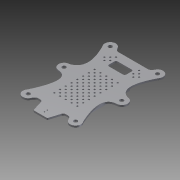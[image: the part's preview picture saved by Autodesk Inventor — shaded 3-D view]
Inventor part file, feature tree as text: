
AUTODESK INVENTOR PART (.ipt)
format: ipt  version: 2015 (Build 190159000, 159)  size: 695,808 bytes
history: native  units: mm
features: sketch x3, extrude x2, hole x2
ambient origin geometry x8: Origin, YZ Plane, XZ Plane, XY Plane, X Axis, Y Axis, Z Axis, Center Point
bodies: Solid1 (feature_tree)
feature tree (7):
  sketch  "Sketch1"  dims[d0=10.0mm d1=6.5mm d2=6.5mm d3=6.5mm d4=6.5mm d5=6.5mm d6=12.0mm d7=2.0mm d8=2.0mm d9=5.0mm d10=5.0mm d11=71.014083mm d12=41.0mm d13=3.0mm d14=3.0mm d15=3.0mm d16=3.0mm d17=3.0mm d18=3.0mm d19=3.0mm d20=3.0mm d21=10.0mm d22=3.0mm d23=3.0mm d24=3.0mm d25=10.0mm d26=12.5mm d27=12.5mm d28=12.5mm d29=12.5mm d30=8.00764mm d31=17.45764mm d32=8.00764mm d33=12.118872mm d34=2.0mm d35=10.0mm d36=10.0mm d37=10.0mm d38=10.0mm d39=10.0mm d40=10.0mm d41=10.0mm d42=10.0mm d43=3.0mm d44=3.0mm d45=3.0mm d46=3.0mm d47=18.0mm d48=5.0mm d49=1.0mm d50=18.0mm d51=18.0mm d52=10.0mm d53=10.0mm d54=10.0mm d55=6.5mm d56=3.0mm d57=3.0mm d58=3.0mm d59=3.0mm d60=3.0mm d61=3.0mm d62=3.0mm d63=10.0mm d64=3.0mm d65=3.0mm d66=3.0mm d67=10.0mm d68=3.0mm d69=3.0mm d70=3.0mm d71=10.0mm d72=3.0mm d73=3.0mm d74=3.0mm d75=10.0mm d76=3.0mm d77=3.0mm d78=3.0mm d79=10.0mm d80=3.0mm d81=3.0mm d82=3.0mm d83=10.0mm d84=3.0mm d85=3.0mm d86=3.0mm d87=10.0mm d88=3.0mm d89=3.0mm d90=3.0mm d91=10.0mm d92=3.0mm d93=3.0mm d94=3.0mm d95=10.0mm d96=3.0mm d97=0.0mm]
  extrude  "Extrusion1"  Depth=10.0mm TaperAngle=0.0deg
  hole  "Hole1"  [1 undecoded]
  hole  "Hole2"  [1 undecoded]
  extrude  "Extrusion2"  [1 undecoded]
  sketch  "Sketch2"  dims[d98=10.0mm d99=6.5mm d100=6.5mm d101=6.5mm d102=6.5mm d103=6.5mm d104=12.0mm d105=2.0mm d106=2.0mm d107=5.0mm d108=5.0mm d109=71.014083mm d110=41.0mm d111=3.0mm d112=3.0mm d113=3.0mm d114=3.0mm d115=3.0mm d116=3.0mm d117=3.0mm d118=3.0mm d119=10.0mm d120=3.0mm d121=3.0mm d122=3.0mm d123=10.0mm d124=12.5mm d125=12.5mm d126=12.5mm d127=12.5mm d128=8.00764mm d129=17.45764mm d130=8.00764mm d131=12.118872mm d132=2.0mm d133=10.0mm d134=10.0mm d135=10.0mm d136=10.0mm d137=10.0mm d138=10.0mm d139=10.0mm d140=10.0mm d141=3.0mm d142=3.0mm d143=3.0mm d144=3.0mm d145=18.0mm d146=5.0mm d147=1.0mm d148=18.0mm d149=18.0mm d150=10.0mm d151=10.0mm d152=10.0mm d153=6.5mm d154=3.0mm d155=3.0mm d156=3.0mm d157=3.0mm d158=3.0mm d159=3.0mm d160=3.0mm d161=10.0mm d162=3.0mm d163=3.0mm d164=3.0mm d165=10.0mm d166=3.0mm d167=3.0mm d168=3.0mm d169=10.0mm d170=3.0mm d171=3.0mm d172=3.0mm d173=10.0mm d174=3.0mm d175=3.0mm d176=3.0mm d177=10.0mm d178=3.0mm d179=3.0mm d180=3.0mm d181=10.0mm d182=3.0mm d183=3.0mm d184=3.0mm d185=10.0mm d186=3.0mm d187=3.0mm d188=3.0mm d189=10.0mm d190=3.0mm d191=3.0mm d192=3.0mm d193=10.0mm d194=6.5mm d195=6.0mm d196=4.0mm d197=2.0mm d198=90.0deg d199=8.0mm d200=20.594885mm]
  sketch  "Sketch3"  dims[d201=10.0mm d202=6.5mm d203=6.5mm d204=6.5mm d205=6.5mm d206=6.5mm d207=12.0mm d208=2.0mm d209=2.0mm d210=5.0mm d211=5.0mm d212=71.014083mm d213=41.0mm d214=3.0mm d215=3.0mm d216=3.0mm d217=3.0mm d218=3.0mm d219=3.0mm d220=3.0mm d221=3.0mm d222=10.0mm d223=3.0mm d224=3.0mm d225=3.0mm d226=10.0mm d227=12.5mm d228=12.5mm d229=12.5mm d230=12.5mm d231=8.00764mm d232=17.45764mm d233=8.00764mm d234=12.118872mm d235=2.0mm d236=10.0mm d237=10.0mm d238=10.0mm d239=10.0mm d240=10.0mm d241=10.0mm d242=10.0mm d243=10.0mm d244=3.0mm d245=3.0mm d246=3.0mm d247=3.0mm d248=18.0mm d249=5.0mm d250=1.0mm d251=18.0mm d252=18.0mm d253=10.0mm d254=10.0mm d255=10.0mm d256=6.5mm d257=3.0mm d258=3.0mm d259=3.0mm d260=3.0mm d261=3.0mm d262=3.0mm d263=3.0mm d264=10.0mm d265=3.0mm d266=3.0mm d267=3.0mm d268=10.0mm d269=3.0mm d270=3.0mm d271=3.0mm d272=10.0mm d273=3.0mm d274=3.0mm d275=3.0mm d276=10.0mm d277=3.0mm d278=3.0mm d279=3.0mm d280=10.0mm d281=3.0mm d282=3.0mm d283=3.0mm d284=10.0mm d285=3.0mm d286=3.0mm d287=3.0mm d288=10.0mm d289=3.0mm d290=3.0mm d291=3.0mm d292=10.0mm d293=3.0mm d294=3.0mm d295=3.0mm d296=10.0mm d297=3.0mm d298=6.0mm d299=4.0mm d300=2.0mm d301=90.0deg d302=8.0mm d303=20.594885mm d304=10.0mm d305=0.0mm d306=19.985917mm]
note: 3 required parameter values undecoded (feature->parameter linkage not recoverable at this tier; creation-order binding heuristic only, values carry confidence <= 0.55)
